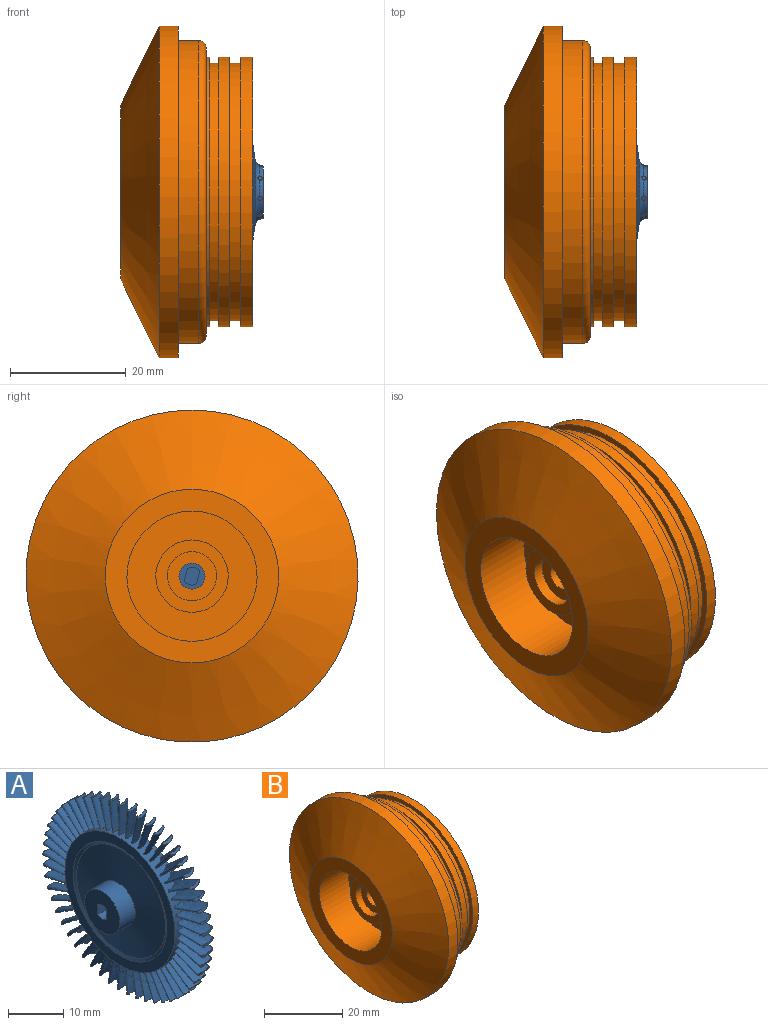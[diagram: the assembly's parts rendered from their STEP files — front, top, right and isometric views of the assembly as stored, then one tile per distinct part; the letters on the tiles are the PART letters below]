
ASSEMBLY  parts=2 mates=1
PART A: 146 faces, bbox 10.2x40.9x40.9 mm
  f0: cylinder r=0.38mm len=0.77mm, axis (0,0.71,0.71), area 0.5mm2, adj f1,f128,f129
  f1: plane 0.75x0.53mm, normal (0,0.71,0.71), area 0.4mm2, adj f0
  f2: cylinder r=0.38mm len=0.75mm, axis (0,1,0), area 0.5mm2, adj f3,f128,f129
  f3: plane 0.75x0.75mm, normal (0,1,0), area 0.4mm2, adj f2
  f4: cylinder r=0.38mm len=0.77mm, axis (0,0.71,-0.71), area 0.5mm2, adj f5,f128,f129
  f5: plane 0.75x0.53mm, normal (0,0.71,-0.71), area 0.4mm2, adj f4
  f6: cylinder r=0.38mm len=0.75mm, axis (0,0,-1), area 0.5mm2, adj f7,f128,f129
  f7: plane 0.75x0.75mm, normal (0,0,-1), area 0.4mm2, adj f6
  f8: cylinder r=0.38mm len=0.77mm, axis (0,-0.71,-0.71), area 0.5mm2, adj f9,f128,f129
  f9: plane 0.75x0.53mm, normal (0,-0.71,-0.71), area 0.4mm2, adj f8
  f10: cylinder r=0.38mm len=0.75mm, axis (0,-1,0), area 0.5mm2, adj f11,f128,f129
  f11: plane 0.75x0.75mm, normal (0,-1,0), area 0.4mm2, adj f10
  f12: cylinder r=0.38mm len=0.77mm, axis (0,-0.71,0.71), area 0.5mm2, adj f13,f128,f129
  f13: plane 0.75x0.53mm, normal (0,-0.71,0.71), area 0.4mm2, adj f12
  f14: plane 2.85x1.11mm, normal (0,-0.99,-0.12), area 1.3mm2, adj f15
  f15: bspline ~6.39x2.84mm, area 41mm2, adj f14,f121
  f16: plane 2.85x1.08mm, normal (0,-0.97,-0.23), area 1.3mm2, adj f17
  f17: bspline ~6.34x3.11mm, area 41mm2, adj f16,f121
  f18: plane 2.85x1.05mm, normal (0,-0.94,-0.34), area 1.3mm2, adj f19
  f19: bspline ~6.21x3.76mm, area 41mm2, adj f18,f121
  f20: plane 2.85x1mm, normal (0,-0.89,-0.45), area 1.3mm2, adj f21
  f21: bspline ~6x4.36mm, area 41mm2, adj f20,f121
  f22: plane 2.85x0.94mm, normal (0,-0.84,-0.55), area 1.3mm2, adj f23
  f23: bspline ~5.7x4.9mm, area 41mm2, adj f22,f121
  f24: plane 2.85x0.86mm, normal (0,-0.77,-0.64), area 1.3mm2, adj f25
  f25: bspline ~5.38x5.32mm, area 41mm2, adj f24,f121
  f26: plane 2.85x0.82mm, normal (0,-0.69,-0.73), area 1.3mm2, adj f27
  f27: bspline ~5.78x4.88mm, area 41mm2, adj f26,f121
  f28: plane 2.85x0.9mm, normal (0,-0.6,-0.8), area 1.3mm2, adj f29
  f29: bspline ~6.1x4.37mm, area 41mm2, adj f28,f121
  f30: plane 2.85x0.97mm, normal (0,-0.5,-0.87), area 1.3mm2, adj f31
  f31: bspline ~6.34x3.8mm, area 41mm2, adj f30,f121
  f32: plane 2.85x1.02mm, normal (0,-0.4,-0.92), area 1.3mm2, adj f33
  f33: bspline ~6.5x3.17mm, area 41mm2, adj f32,f121
  f34: plane 2.85x1.07mm, normal (0,-0.29,-0.96), area 1.3mm2, adj f35
  f35: bspline ~6.57x2.84mm, area 41mm2, adj f34,f121
  f36: plane 2.85x1.1mm, normal (0,-0.17,-0.98), area 1.3mm2, adj f37
  f37: bspline ~6.55x2.84mm, area 41mm2, adj f36,f121
  f38: plane 2.85x1.11mm, normal (0,-0.06,-1), area 1.3mm2, adj f39
  f39: bspline ~6.44x2.84mm, area 41mm2, adj f38,f121
  f40: plane 2.85x1.11mm, normal (0,0.06,-1), area 1.3mm2, adj f41
  f41: bspline ~6.38x2.84mm, area 41mm2, adj f40,f121
  f42: plane 2.85x1.1mm, normal (0,0.17,-0.98), area 1.3mm2, adj f43
  f43: bspline ~6.38x2.84mm, area 41mm2, adj f42,f121
  f44: plane 2.85x1.07mm, normal (0,0.29,-0.96), area 1.3mm2, adj f45
  f45: bspline ~6.29x3.44mm, area 41mm2, adj f44,f121
  f46: plane 2.85x1.02mm, normal (0,0.4,-0.92), area 1.3mm2, adj f47
  f47: bspline ~6.11x4.07mm, area 41mm2, adj f46,f121
  f48: plane 2.85x0.97mm, normal (0,0.5,-0.87), area 1.3mm2, adj f49
  f49: bspline ~5.86x4.64mm, area 41mm2, adj f48,f121
  f50: plane 2.85x0.9mm, normal (0,0.6,-0.8), area 1.3mm2, adj f51
  f51: bspline ~5.52x5.15mm, area 41mm2, adj f50,f121
  f52: plane 2.85x0.82mm, normal (0,0.69,-0.73), area 1.3mm2, adj f53
  f53: bspline ~5.59x5.11mm, area 41mm2, adj f52,f121
  f54: plane 2.85x0.86mm, normal (0,0.77,-0.64), area 1.3mm2, adj f55
  f55: bspline ~5.95x4.63mm, area 41mm2, adj f54,f121
  f56: plane 2.85x0.94mm, normal (0,0.84,-0.55), area 1.3mm2, adj f57
  f57: bspline ~6.23x4.09mm, area 41mm2, adj f56,f121
  f58: plane 2.85x1mm, normal (0,0.89,-0.45), area 1.3mm2, adj f59
  f59: bspline ~6.43x3.49mm, area 41mm2, adj f58,f121
  f60: plane 2.85x1.05mm, normal (0,0.94,-0.34), area 1.3mm2, adj f61
  f61: bspline ~6.54x2.84mm, area 41mm2, adj f60,f121
  f62: plane 2.85x1.08mm, normal (0,0.97,-0.23), area 1.3mm2, adj f63
  f63: bspline ~6.57x2.84mm, area 41mm2, adj f62,f121
  f64: plane 2.85x1.11mm, normal (0,0.99,-0.12), area 1.3mm2, adj f65
  f65: bspline ~6.5x2.84mm, area 41mm2, adj f64,f121
  f66: plane 2.85x1.11mm, normal (0,1,0), area 1.3mm2, adj f67
  f67: bspline ~6.35x2.84mm, area 41mm2, adj f66,f121
  f68: plane 2.85x1.11mm, normal (0,0.99,0.12), area 1.3mm2, adj f69
  f69: bspline ~6.39x2.84mm, area 41mm2, adj f68,f121
  f70: plane 2.85x1.08mm, normal (0,0.97,0.23), area 1.3mm2, adj f71
  f71: bspline ~6.34x3.11mm, area 41mm2, adj f70,f121
  f72: plane 2.85x1.05mm, normal (0,0.94,0.34), area 1.3mm2, adj f73
  f73: bspline ~6.21x3.76mm, area 41mm2, adj f72,f121
  f74: plane 2.85x1mm, normal (0,0.89,0.45), area 1.3mm2, adj f75
  f75: bspline ~6x4.36mm, area 41mm2, adj f74,f121
  f76: plane 2.85x0.94mm, normal (0,0.84,0.55), area 1.3mm2, adj f77
  f77: bspline ~5.7x4.9mm, area 41mm2, adj f76,f121
  f78: plane 2.85x0.86mm, normal (0,0.77,0.64), area 1.3mm2, adj f79
  f79: bspline ~5.38x5.32mm, area 41mm2, adj f78,f121
  f80: plane 2.85x0.82mm, normal (0,0.69,0.73), area 1.3mm2, adj f81
  f81: bspline ~5.78x4.88mm, area 41mm2, adj f80,f121
  f82: plane 2.85x0.9mm, normal (0,0.6,0.8), area 1.3mm2, adj f83
  f83: bspline ~6.1x4.37mm, area 41mm2, adj f82,f121
  f84: plane 2.85x0.97mm, normal (0,0.5,0.87), area 1.3mm2, adj f85
  f85: bspline ~6.34x3.8mm, area 41mm2, adj f84,f121
  f86: plane 2.85x1.02mm, normal (0,0.4,0.92), area 1.3mm2, adj f87
  f87: bspline ~6.5x3.17mm, area 41mm2, adj f86,f121
  f88: plane 2.85x1.07mm, normal (0,0.29,0.96), area 1.3mm2, adj f89
  f89: bspline ~6.57x2.84mm, area 41mm2, adj f88,f121
  f90: plane 2.85x1.1mm, normal (0,0.17,0.98), area 1.3mm2, adj f91
  f91: bspline ~6.55x2.84mm, area 41mm2, adj f90,f121
  f92: plane 2.85x1.11mm, normal (0,0.06,1), area 1.3mm2, adj f93
  f93: bspline ~6.44x2.84mm, area 41mm2, adj f92,f121
  f94: plane 2.85x1.11mm, normal (0,-0.06,1), area 1.3mm2, adj f95
  f95: bspline ~6.4x2.84mm, area 41.1mm2, adj f94,f121
  f96: plane 2.85x1.1mm, normal (0,-0.17,0.98), area 1.3mm2, adj f97
  f97: bspline ~6.38x2.84mm, area 41mm2, adj f96,f121
  f98: plane 2.85x1.07mm, normal (0,-0.29,0.96), area 1.3mm2, adj f99
  f99: bspline ~6.29x3.44mm, area 41mm2, adj f98,f121
  f100: plane 2.85x1.02mm, normal (0,-0.4,0.92), area 1.3mm2, adj f101
  f101: bspline ~6.11x4.07mm, area 41mm2, adj f100,f121
  f102: plane 2.85x0.97mm, normal (0,-0.5,0.87), area 1.3mm2, adj f103
  f103: bspline ~5.86x4.64mm, area 41mm2, adj f102,f121
  f104: plane 2.85x0.9mm, normal (0,-0.6,0.8), area 1.3mm2, adj f105
  f105: bspline ~5.52x5.15mm, area 41mm2, adj f104,f121
  f106: plane 2.85x0.82mm, normal (0,-0.69,0.73), area 1.3mm2, adj f107
  f107: bspline ~5.59x5.11mm, area 41mm2, adj f106,f121
  f108: plane 2.85x0.86mm, normal (0,-0.77,0.64), area 1.3mm2, adj f109
  f109: bspline ~5.95x4.63mm, area 41mm2, adj f108,f121
  f110: plane 2.85x0.94mm, normal (0,-0.84,0.55), area 1.3mm2, adj f111
  f111: bspline ~6.23x4.09mm, area 41mm2, adj f110,f121
  f112: plane 2.85x1mm, normal (0,-0.89,0.45), area 1.3mm2, adj f113
  f113: bspline ~6.43x3.49mm, area 41mm2, adj f112,f121
  f114: plane 2.85x1.05mm, normal (0,-0.94,0.34), area 1.3mm2, adj f115
  f115: bspline ~6.54x2.84mm, area 41mm2, adj f114,f121
  f116: plane 2.85x1.08mm, normal (0,-0.97,0.23), area 1.3mm2, adj f117
  f117: bspline ~6.57x2.84mm, area 41mm2, adj f116,f121
  f118: plane 2.85x1.11mm, normal (0,-0.99,0.12), area 1.3mm2, adj f119
  f119: bspline ~6.5x2.84mm, area 41mm2, adj f118,f121
  f120: plane 28.2x28.2mm, normal (-1,0,0), area 172.2mm2, adj f121,f136
  f121: cylinder r=14.1mm len=28.2mm, axis (-1,0,0), area 253.6mm2, adj f15,f17,f19,f21,f23,f25,f27,f29
  f122: plane 28.2x28.2mm, normal (1,0,0), area 17.6mm2, adj f121,f123
  f123: cylinder r=13.9mm len=27.8mm, axis (-1,0,0), area 17.5mm2, adj f122,f124
  f124: plane 27.8x27.8mm, normal (1,0,0), area 139.4mm2, adj f123,f125
  f125: cone r=12.18mm half-angle=33.7deg, axis (1,0,0), area 3.2mm2, adj f124,f126
  f126: torus R=11.76mm, axis (-1,0,0), area 42.6mm2, adj f125,f127
  f127: cone r=5.52mm half-angle=81.3deg, axis (-1,0,0), area 337mm2, adj f126,f128
  f128: torus R=5.67mm, axis (-1,0,0), area 34.5mm2, adj f0,f2,f4,f6,f8,f10,f12,f127
  f129: cone r=4.72mm half-angle=17deg, axis (-1,0,0), area 19.1mm2, adj f0,f2,f4,f6,f8,f10,f12,f128
  f130: plane 9x9mm, normal (1,0,0), area 31.9mm2, adj f129,f131
  f131: cylinder r=3.17mm len=6.35mm, axis (-1,0,0), area 21.1mm2, adj f130,f132
  f132: plane 6.35x6.35mm, normal (1,0,0), area 31.7mm2, adj f131
  f133: plane 9x9mm, normal (-1,0,0), area 57.4mm2, adj f134,f139,f140,f141,f142
  f134: cylinder r=4.5mm len=9mm, axis (-1,0,0), area 113.1mm2, adj f133,f135
  f135: cone r=11.4mm half-angle=83deg, axis (1,0,0), area 347.3mm2, adj f134,f136
  f136: cone r=12mm half-angle=63.4deg, axis (-1,0,0), area 49.3mm2, adj f120,f135
  f137: plane 2.85x1.11mm, normal (0,-1,0), area 1.3mm2, adj f138
  f138: bspline ~6.35x2.84mm, area 41mm2, adj f121,f137
  f139: plane 4x2.18mm, normal (0,-1,0), area 8.7mm2, adj f133,f140,f142,f143
  f140: cylinder r=1.55mm len=4mm, axis (-1,0,0), area 9.8mm2, adj f133,f139,f141,f143
  f141: plane 4x2.18mm, normal (0,1,0), area 8.7mm2, adj f133,f140,f142,f143
  f142: cylinder r=1.55mm len=4mm, axis (-1,0,0), area 9.8mm2, adj f133,f139,f141,f143
  f143: plane 3.1x2.2mm, normal (-1,0,0), area 6.2mm2, adj f139,f140,f141,f142
  f144: cylinder r=0.38mm len=0.75mm, axis (0,0,1), area 0.4mm2, adj f128,f129,f145
  f145: plane 0.75x0.75mm, normal (0,0,1), area 0.4mm2, adj f144
PART B: 89 faces, bbox 22.8x57.4x57.4 mm
  f0: extruded ~7.05x2.45mm, area 38.9mm2, adj f53,f57
  f1: extruded ~7x2.45mm, area 38.9mm2, adj f53,f57
  f2: extruded ~6.85x3.11mm, area 38.9mm2, adj f53,f57
  f3: extruded ~6.61x3.83mm, area 38.9mm2, adj f53,f57
  f4: extruded ~6.28x4.49mm, area 38.9mm2, adj f53,f57
  f5: extruded ~5.86x5.09mm, area 38.9mm2, adj f53,f57
  f6: extruded ~5.62x5.37mm, area 38.9mm2, adj f53,f57
  f7: extruded ~6.08x4.8mm, area 38.9mm2, adj f53,f57
  f8: extruded ~6.45x4.17mm, area 38.9mm2, adj f53,f57
  f9: extruded ~6.74x3.48mm, area 38.9mm2, adj f53,f57
  f10: extruded ~6.94x2.74mm, area 38.9mm2, adj f53,f57
  f11: extruded ~7.04x2.45mm, area 38.9mm2, adj f53,f57
  f12: extruded ~7.04x2.45mm, area 38.9mm2, adj f53,f57
  f13: extruded ~7.04x2.45mm, area 38.9mm2, adj f53,f57
  f14: extruded ~7.04x2.45mm, area 38.9mm2, adj f53,f57
  f15: extruded ~6.94x2.74mm, area 38.9mm2, adj f53,f57
  f16: extruded ~6.74x3.48mm, area 38.9mm2, adj f53,f57
  f17: extruded ~6.45x4.17mm, area 38.9mm2, adj f53,f57
  f18: extruded ~6.08x4.8mm, area 38.9mm2, adj f53,f57
  f19: extruded ~5.62x5.37mm, area 38.9mm2, adj f53,f57
  f20: extruded ~5.86x5.09mm, area 38.9mm2, adj f53,f57
  f21: extruded ~6.28x4.49mm, area 38.9mm2, adj f53,f57
  f22: extruded ~6.61x3.83mm, area 38.9mm2, adj f53,f57
  f23: extruded ~6.85x3.11mm, area 38.9mm2, adj f53,f57
  f24: extruded ~7x2.45mm, area 38.9mm2, adj f53,f57
  f25: extruded ~7.05x2.45mm, area 38.9mm2, adj f53,f57
  f26: extruded ~7.01x2.45mm, area 38.9mm2, adj f53,f57
  f27: extruded ~7.05x2.45mm, area 38.9mm2, adj f53,f57
  f28: extruded ~7x2.45mm, area 38.9mm2, adj f53,f57
  f29: extruded ~6.85x3.11mm, area 38.9mm2, adj f53,f57
  f30: extruded ~6.61x3.83mm, area 38.9mm2, adj f53,f57
  f31: extruded ~6.28x4.49mm, area 38.9mm2, adj f53,f57
  f32: extruded ~5.86x5.09mm, area 38.9mm2, adj f53,f57
  f33: extruded ~5.62x5.37mm, area 38.9mm2, adj f53,f57
  f34: extruded ~6.08x4.8mm, area 38.9mm2, adj f53,f57
  f35: extruded ~6.45x4.17mm, area 38.9mm2, adj f53,f57
  f36: extruded ~6.74x3.48mm, area 38.9mm2, adj f53,f57
  f37: extruded ~6.94x2.74mm, area 38.9mm2, adj f53,f57
  f38: extruded ~7.04x2.45mm, area 38.9mm2, adj f53,f57
  f39: extruded ~7.04x2.45mm, area 38.9mm2, adj f53,f57
  f40: extruded ~7.04x2.45mm, area 38.9mm2, adj f53,f57
  f41: extruded ~7.04x2.45mm, area 38.9mm2, adj f53,f57
  f42: extruded ~6.94x2.74mm, area 38.9mm2, adj f53,f57
  f43: extruded ~6.74x3.48mm, area 38.9mm2, adj f53,f57
  f44: extruded ~6.45x4.17mm, area 38.9mm2, adj f53,f57
  f45: extruded ~6.08x4.8mm, area 38.9mm2, adj f53,f57
  f46: extruded ~5.62x5.37mm, area 38.9mm2, adj f53,f57
  f47: extruded ~5.86x5.09mm, area 38.9mm2, adj f53,f57
  f48: extruded ~6.28x4.49mm, area 38.9mm2, adj f53,f57
  f49: extruded ~6.61x3.83mm, area 38.9mm2, adj f53,f57
  f50: extruded ~6.85x3.11mm, area 38.9mm2, adj f53,f57
  f51: extruded ~7x2.45mm, area 38.9mm2, adj f53,f57
  f52: extruded ~7.05x2.45mm, area 38.9mm2, adj f53,f57
  f53: cylinder r=14mm len=28mm, axis (-1,0,0), area 1258.3mm2, adj f0,f1,f2,f3,f4,f5,f6,f7
  f54: plane 30x30mm, normal (1,0,0), area 91.1mm2, adj f53,f55
  f55: cone r=24.4mm half-angle=64deg, axis (1,0,0), area 1294.3mm2, adj f54,f56
  f56: cone r=21mm half-angle=26deg, axis (-1,0,0), area 1105.7mm2, adj f55,f57
  f57: cylinder r=21mm len=42mm, axis (-1,0,0), area 1051.9mm2, adj f0,f1,f2,f3,f4,f5,f6,f7
  f58: plane 46.6x46.6mm, normal (1,0,0), area 320.1mm2, adj f57,f59
  f59: cylinder r=23.3mm len=46.6mm, axis (-1,0,0), area 313.2mm2, adj f58,f60
  f60: plane 46.6x46.6mm, normal (-1,0,0), area 150.3mm2, adj f59,f61
  f61: cylinder r=22.25mm len=44.5mm, axis (-1,0,0), area 265.6mm2, adj f60,f62
  f62: plane 46.6x46.6mm, normal (1,0,0), area 150.3mm2, adj f61,f63
  f63: cylinder r=23.3mm len=46.6mm, axis (-1,0,0), area 278.2mm2, adj f62,f64
  f64: plane 46.6x46.6mm, normal (-1,0,0), area 150.3mm2, adj f63,f65
  f65: cylinder r=22.25mm len=44.5mm, axis (-1,0,0), area 209.7mm2, adj f64,f66
  f66: plane 46.6x46.6mm, normal (1,0,0), area 150.3mm2, adj f65,f67
  f67: cylinder r=23.3mm len=46.6mm, axis (-1,0,0), area 89.3mm2, adj f66,f68
  f68: plane 49.86x49.86mm, normal (1,0,0), area 246.7mm2, adj f67,f69
  f69: torus R=24.93mm, axis (-1,0,0), area 317.4mm2, adj f68,f70
  f70: cylinder r=26.18mm len=52.36mm, axis (-1,0,0), area 616.8mm2, adj f69,f71
  f71: plane 55.22x55.22mm, normal (1,0,0), area 241.6mm2, adj f70,f72
  f72: cylinder r=27.61mm len=55.22mm, axis (-1,0,0), area 34.7mm2, adj f71,f73
  f73: plane 57.4x57.4mm, normal (1,0,0), area 193.1mm2, adj f72,f74
  f74: cylinder r=28.7mm len=57.4mm, axis (-1,0,0), area 595.4mm2, adj f73,f75
  f75: cone r=28.7mm half-angle=64deg, axis (1,0,0), area 2092.6mm2, adj f74,f76
  f76: plane 30x30mm, normal (-1,0,0), area 309.3mm2, adj f75,f77
  f77: cylinder r=11.25mm len=22.5mm, axis (-1,0,0), area 748mm2, adj f76,f78
  f78: plane 22.5x22.5mm, normal (-1,0,0), area 274.9mm2, adj f77,f79
  f79: cylinder r=6.25mm len=12.5mm, axis (-1,0,0), area 176.7mm2, adj f78,f80
  f80: plane 12.5x12.5mm, normal (-1,0,0), area 66mm2, adj f79,f81
  f81: cylinder r=4.25mm len=8.5mm, axis (-1,0,0), area 53.4mm2, adj f80,f82
  f82: plane 8.5x8.5mm, normal (-1,0,0), area 40.8mm2, adj f81,f83
  f83: cylinder r=2.25mm len=5mm, axis (-1,0,0), area 70.7mm2, adj f82,f84
  f84: plane 10x10mm, normal (1,0,0), area 62.6mm2, adj f83,f85
  f85: cylinder r=5mm len=10mm, axis (-1,0,0), area 128.8mm2, adj f84,f86
  f86: cone r=5mm half-angle=82.4deg, axis (1,0,0), area 206.8mm2, adj f85,f87
  f87: plane 28x28mm, normal (1,0,0), area 332.2mm2, adj f53,f86
  f88: extruded ~7.01x2.45mm, area 38.9mm2, adj f53,f57
PLACE A rot(axis=(1,0,0),13.6deg) t=(55.85,34.05,-12.97)mm
PLACE B t=(54.98,34.05,-12.97)mm fixed
MATE cylindrical B.f53 <-> A.f121  axis (-1,0,0) through (88.23,34.05,-12.97)mm
